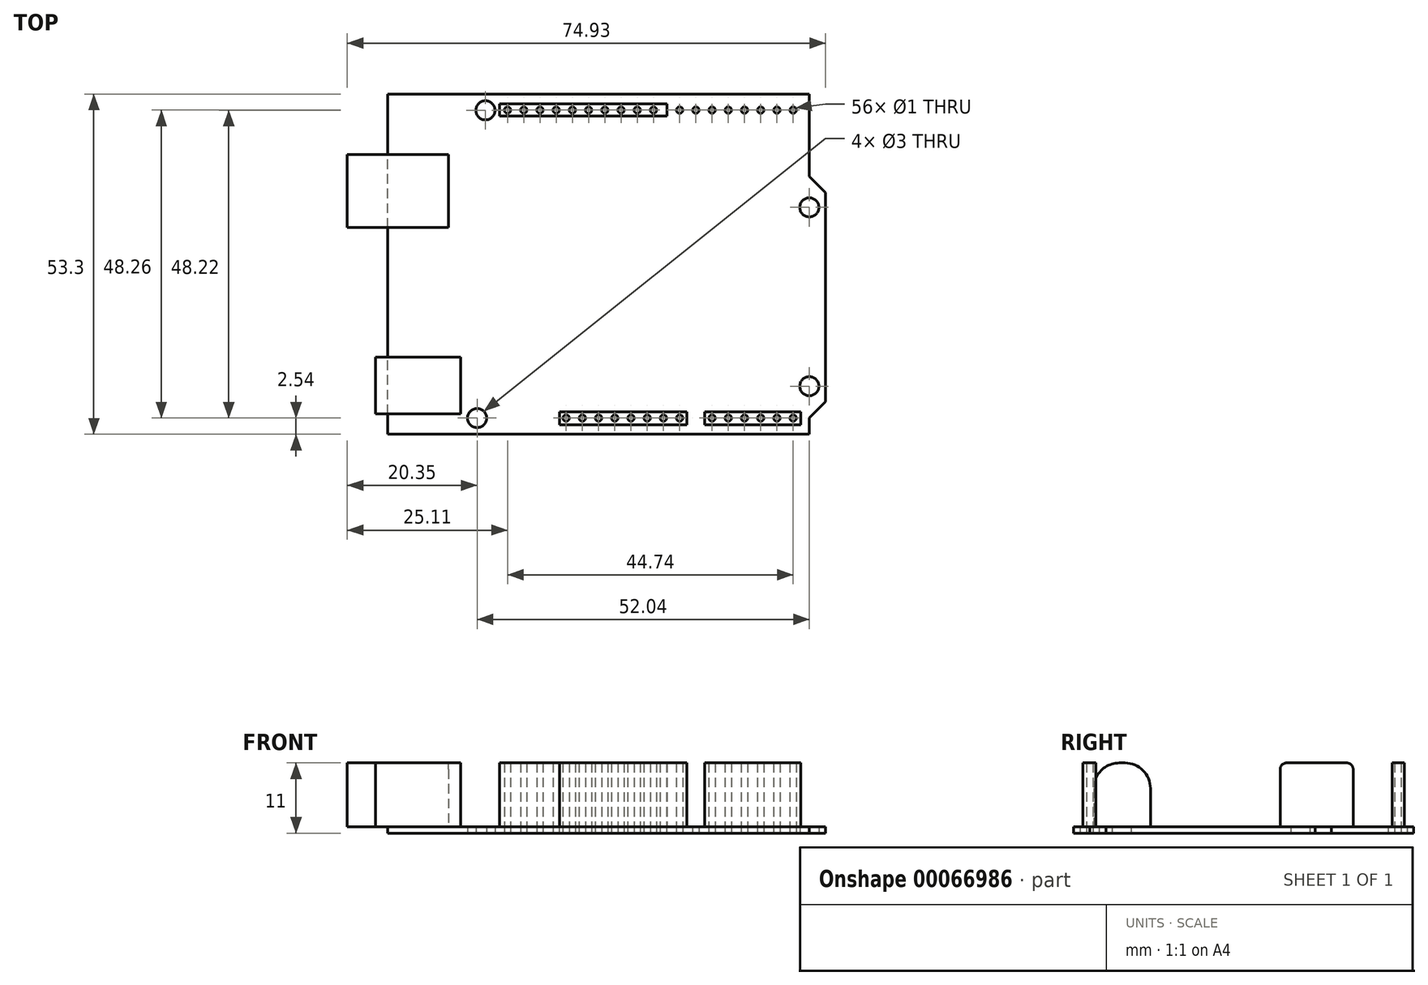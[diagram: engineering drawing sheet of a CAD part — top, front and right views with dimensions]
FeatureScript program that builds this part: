
annotation { "Feature Type Name" : "Feature", "Feature Type Description" : "" }
export const myFeature = defineFeature(function(context is Context, id is Id, definition is map)
    precondition{}
    {
        {
            var Q0;
            Q0=qCreatedBy(makeId("Top.planeOp"),FACE);
            var sketch = newSketch(context, id + "F0", { "sketchPlane" : qUnion([Q0])});
            skLineSegment(sketch, "E0.bottom", {"start": v(0, 0) * mm, "end": v(66.04, 0) * mm});
            skLineSegment(sketch, "E0.top", {"start": v(0, 53.3) * mm, "end": v(66.04, 53.3) * mm});
            skLineSegment(sketch, "E0.left", {"start": v(0, 0) * mm, "end": v(0, 53.3) * mm});
            skLineSegment(sketch, "E1.0", {"start": v(66.04, 0) * mm, "end": v(66.04, 2.54) * mm});
            skLineSegment(sketch, "E2", {"start": v(66.04, 2.54) * mm, "end": v(68.58, 5.08) * mm});
            skCircle(sketch, "E3", {"center": v(14, 2.54) * mm, "radius": 1.5 * mm});
            skCircle(sketch, "E4", {"center": v(66.04, 7.53) * mm, "radius": 1.5 * mm});
            skCircle(sketch, "E5", {"center": v(15.3, 50.76) * mm, "radius": 1.5 * mm});
            skCircle(sketch, "E6", {"center": v(66.04, 35.56) * mm, "radius": 1.5 * mm});
            skLineSegment(sketch, "E7.trimOffspring", {"start": v(68.58, 5.08) * mm, "end": v(68.58, 37.85) * mm});
            skLineSegment(sketch, "E8", {"start": v(66.04, 40.4) * mm, "end": v(68.58, 37.85) * mm});
            skLineSegment(sketch, "E9.trimOffspring", {"start": v(66.04, 40.4) * mm, "end": v(66.04, 53.34) * mm});
            skCircle(sketch, "E10", {"center": v(27.94, 2.54) * mm, "radius": 0.5 * mm});
            skCircle(sketch, "E11.1.0.0", {"center": v(30.48, 2.54) * mm, "radius": 0.5 * mm});
            skCircle(sketch, "E11.2.0.0", {"center": v(33.02, 2.54) * mm, "radius": 0.5 * mm});
            skCircle(sketch, "E11.3.0.0", {"center": v(35.56, 2.54) * mm, "radius": 0.5 * mm});
            skCircle(sketch, "E11.4.0.0", {"center": v(38.1, 2.54) * mm, "radius": 0.5 * mm});
            skCircle(sketch, "E11.5.0.0", {"center": v(40.64, 2.54) * mm, "radius": 0.5 * mm});
            skCircle(sketch, "E11.6.0.0", {"center": v(43.18, 2.54) * mm, "radius": 0.5 * mm});
            skCircle(sketch, "E11.7.0.0", {"center": v(45.72, 2.54) * mm, "radius": 0.5 * mm});
            skCircle(sketch, "E11.9.0.0", {"center": v(50.8, 2.54) * mm, "radius": 0.5 * mm});
            skCircle(sketch, "E11.10.0.0", {"center": v(53.34, 2.54) * mm, "radius": 0.5 * mm});
            skCircle(sketch, "E11.11.0.0", {"center": v(55.88, 2.54) * mm, "radius": 0.5 * mm});
            skCircle(sketch, "E11.12.0.0", {"center": v(58.42, 2.54) * mm, "radius": 0.5 * mm});
            skCircle(sketch, "E11.13.0.0", {"center": v(60.96, 2.54) * mm, "radius": 0.5 * mm});
            skCircle(sketch, "E11.14.0.0", {"center": v(63.5, 2.54) * mm, "radius": 0.5 * mm});
            skCircle(sketch, "E12", {"center": v(18.76, 50.8) * mm, "radius": 0.5 * mm});
            skCircle(sketch, "E13.1.0.0", {"center": v(21.3, 50.8) * mm, "radius": 0.5 * mm});
            skCircle(sketch, "E13.2.0.0", {"center": v(23.84, 50.8) * mm, "radius": 0.5 * mm});
            skCircle(sketch, "E13.3.0.0", {"center": v(26.38, 50.8) * mm, "radius": 0.5 * mm});
            skCircle(sketch, "E13.4.0.0", {"center": v(28.92, 50.8) * mm, "radius": 0.5 * mm});
            skCircle(sketch, "E13.5.0.0", {"center": v(31.46, 50.8) * mm, "radius": 0.5 * mm});
            skCircle(sketch, "E13.6.0.0", {"center": v(34, 50.8) * mm, "radius": 0.5 * mm});
            skCircle(sketch, "E13.7.0.0", {"center": v(36.54, 50.8) * mm, "radius": 0.5 * mm});
            skCircle(sketch, "E13.8.0.0", {"center": v(39.08, 50.8) * mm, "radius": 0.5 * mm});
            skCircle(sketch, "E13.9.0.0", {"center": v(41.62, 50.8) * mm, "radius": 0.5 * mm});
            skCircle(sketch, "E14", {"center": v(45.72, 50.8) * mm, "radius": 0.5 * mm});
            skCircle(sketch, "E15.1.0.0", {"center": v(48.26, 50.8) * mm, "radius": 0.5 * mm});
            skCircle(sketch, "E15.2.0.0", {"center": v(50.8, 50.8) * mm, "radius": 0.5 * mm});
            skCircle(sketch, "E15.3.0.0", {"center": v(53.34, 50.8) * mm, "radius": 0.5 * mm});
            skCircle(sketch, "E15.4.0.0", {"center": v(55.88, 50.8) * mm, "radius": 0.5 * mm});
            skCircle(sketch, "E15.5.0.0", {"center": v(58.42, 50.8) * mm, "radius": 0.5 * mm});
            skCircle(sketch, "E15.6.0.0", {"center": v(60.96, 50.8) * mm, "radius": 0.5 * mm});
            skCircle(sketch, "E15.7.0.0", {"center": v(63.5, 50.8) * mm, "radius": 0.5 * mm});
            skLineSegment(sketch, "E16.bottom", {"start": v(11.43, 12.06) * mm, "end": v(-1.9, 12.06) * mm});
            skLineSegment(sketch, "E16.top", {"start": v(11.43, 3.17) * mm, "end": v(-1.9, 3.17) * mm});
            skLineSegment(sketch, "E16.left", {"start": v(11.43, 12.06) * mm, "end": v(11.43, 3.17) * mm});
            skLineSegment(sketch, "E16.right", {"start": v(-1.9, 12.06) * mm, "end": v(-1.9, 3.17) * mm});
            skLineSegment(sketch, "E17.bottom", {"start": v(9.52, 43.81) * mm, "end": v(-6.35, 43.81) * mm});
            skLineSegment(sketch, "E17.top", {"start": v(9.52, 32.38) * mm, "end": v(-6.35, 32.38) * mm});
            skLineSegment(sketch, "E17.left", {"start": v(9.52, 43.81) * mm, "end": v(9.52, 32.38) * mm});
            skLineSegment(sketch, "E17.right", {"start": v(-6.35, 43.81) * mm, "end": v(-6.35, 32.38) * mm});
            skLineSegment(sketch, "E18", {"start": v(-6.35, 22.22) * mm, "end": v(7.42, 22.22) * mm, "construction": true});
            skLineSegment(sketch, "E19.bottom", {"start": v(26.91, 1.5) * mm, "end": v(46.85, 1.5) * mm});
            skLineSegment(sketch, "E19.top", {"start": v(26.91, 3.5) * mm, "end": v(46.85, 3.5) * mm});
            skLineSegment(sketch, "E19.left", {"start": v(26.91, 1.5) * mm, "end": v(26.91, 3.5) * mm});
            skLineSegment(sketch, "E19.right", {"start": v(46.85, 1.5) * mm, "end": v(46.85, 3.5) * mm});
            skLineSegment(sketch, "E20.bottom", {"start": v(49.62, 1.5) * mm, "end": v(64.71, 1.5) * mm});
            skLineSegment(sketch, "E20.top", {"start": v(49.62, 3.5) * mm, "end": v(64.71, 3.5) * mm});
            skLineSegment(sketch, "E20.left", {"start": v(49.62, 1.5) * mm, "end": v(49.62, 3.5) * mm});
            skLineSegment(sketch, "E20.right", {"start": v(64.71, 1.5) * mm, "end": v(64.71, 3.5) * mm});
            skLineSegment(sketch, "E21.bottom", {"start": v(17.53, 49.9) * mm, "end": v(43.72, 49.9) * mm});
            skLineSegment(sketch, "E21.top", {"start": v(17.53, 51.8) * mm, "end": v(43.72, 51.8) * mm});
            skLineSegment(sketch, "E21.left", {"start": v(17.53, 49.9) * mm, "end": v(17.53, 51.8) * mm});
            skLineSegment(sketch, "E21.right", {"start": v(43.72, 49.9) * mm, "end": v(43.72, 51.8) * mm});
            skLineSegment(sketch, "E22.bottom", {"start": v(43.72, 49.9) * mm, "end": v(64.71, 49.9) * mm});
            skLineSegment(sketch, "E22.top", {"start": v(43.72, 51.8) * mm, "end": v(64.71, 51.8) * mm});
            skLineSegment(sketch, "E22.right", {"start": v(64.71, 49.9) * mm, "end": v(64.71, 51.8) * mm});
            skLineSegment(sketch, "E23", {"start": v(0, 26.65) * mm, "end": v(68.58, 26.65) * mm, "construction": true});
            skLineSegment(sketch, "E24", {"start": v(33.02, 53.3) * mm, "end": v(34, 0) * mm, "construction": true});
            skSolve(sketch);
        }
        {
            var Q0;
            {var subQ5=sQuery(id+"F0.wireOp",EDGE,"E17.left");Q0=makeQuery(id+"F0.imprint","IMPRINT",FACE,{"disambiguationData":[TD([[makeQuery(id+"F0.imprint","IMPRINT",EDGE,{"derivedFrom":subQ5}),-1.0]])]});}
            var Q1;
            {var subQ5=sQuery(id+"F0.wireOp",EDGE,"E16.left");Q1=makeQuery(id+"F0.imprint","IMPRINT",FACE,{"disambiguationData":[TD([[makeQuery(id+"F0.imprint","IMPRINT",EDGE,{"derivedFrom":subQ5}),-1.0]])]});}
            var Q2;
            Q2=makeQuery(id+"F0.imprint","IMPRINT",FACE,{"disambiguationData":[TD([[makeQuery(id+"F0.imprint","IMPRINT",EDGE,{"derivedFrom":sQuery(id+"F0.wireOp",EDGE,"E10")}),-1.0]])]});
            var Q3;
            Q3=makeQuery(id+"F0.imprint","IMPRINT",FACE,{"disambiguationData":[TD([[makeQuery(id+"F0.imprint","IMPRINT",EDGE,{"derivedFrom":sQuery(id+"F0.wireOp",EDGE,"E12")}),-1.0]])]});
            var Q4;
            Q4=makeQuery(id+"F0.imprint","IMPRINT",FACE,{"disambiguationData":[TD([[makeQuery(id+"F0.imprint","IMPRINT",EDGE,{"derivedFrom":sQuery(id+"F0.wireOp",EDGE,"E14")}),-1.0]])]});
            var Q5;
            {var subQ12=sQuery(id+"F0.wireOp",EDGE,"E0.bottom");Q5=makeQuery(id+"F0.imprint","IMPRINT",FACE,{"disambiguationData":[TD([[makeQuery(id+"F0.imprint","IMPRINT",EDGE,{"derivedFrom":subQ12}),1.0]])]});}
            var Q6;
            Q6=makeQuery(id+"F0.imprint","IMPRINT",FACE,{"disambiguationData":[TD([[makeQuery(id+"F0.imprint","IMPRINT",EDGE,{"derivedFrom":sQuery(id+"F0.wireOp",EDGE,"E11.9.0.0")}),-1.0]])]});
            extrude(context, id + "F1", {"entities" : qUnion([Q0, Q1, Q2, Q3, Q4, Q5, Q6]), "depth" : 1 * mm});
        }
        {
            var Q0;
            Q0=makeQuery(id+"F1.opExtrude","CAP_FACE",FACE,{"disambiguationData":[OSD([sQuery(id+"F0.wireOp",EDGE,"E0.bottom"),sQuery(id+"F0.wireOp",EDGE,"E0.top"),sQuery(id+"F0.wireOp",EDGE,"E0.left"),sQuery(id+"F0.wireOp",EDGE,"E1.0"),sQuery(id+"F0.wireOp",EDGE,"E2"),sQuery(id+"F0.wireOp",EDGE,"E3"),sQuery(id+"F0.wireOp",EDGE,"E4"),sQuery(id+"F0.wireOp",EDGE,"E5"),sQuery(id+"F0.wireOp",EDGE,"E6"),sQuery(id+"F0.wireOp",EDGE,"E7.trimOffspring"),sQuery(id+"F0.wireOp",EDGE,"E8"),sQuery(id+"F0.wireOp",EDGE,"E9.trimOffspring"),sQuery(id+"F0.wireOp",EDGE,"E10"),sQuery(id+"F0.wireOp",EDGE,"E11.1.0.0"),sQuery(id+"F0.wireOp",EDGE,"E11.2.0.0"),sQuery(id+"F0.wireOp",EDGE,"E11.3.0.0"),sQuery(id+"F0.wireOp",EDGE,"E11.4.0.0"),sQuery(id+"F0.wireOp",EDGE,"E11.5.0.0"),sQuery(id+"F0.wireOp",EDGE,"E11.6.0.0"),sQuery(id+"F0.wireOp",EDGE,"E11.7.0.0"),sQuery(id+"F0.wireOp",EDGE,"E11.9.0.0"),sQuery(id+"F0.wireOp",EDGE,"E11.10.0.0"),sQuery(id+"F0.wireOp",EDGE,"E11.11.0.0"),sQuery(id+"F0.wireOp",EDGE,"E11.12.0.0"),sQuery(id+"F0.wireOp",EDGE,"E11.13.0.0"),sQuery(id+"F0.wireOp",EDGE,"E11.14.0.0"),sQuery(id+"F0.wireOp",EDGE,"E12"),sQuery(id+"F0.wireOp",EDGE,"E13.1.0.0"),sQuery(id+"F0.wireOp",EDGE,"E13.2.0.0"),sQuery(id+"F0.wireOp",EDGE,"E13.3.0.0"),sQuery(id+"F0.wireOp",EDGE,"E13.4.0.0"),sQuery(id+"F0.wireOp",EDGE,"E13.5.0.0"),sQuery(id+"F0.wireOp",EDGE,"E13.6.0.0"),sQuery(id+"F0.wireOp",EDGE,"E13.7.0.0"),sQuery(id+"F0.wireOp",EDGE,"E13.8.0.0"),sQuery(id+"F0.wireOp",EDGE,"E13.9.0.0"),sQuery(id+"F0.wireOp",EDGE,"E14"),sQuery(id+"F0.wireOp",EDGE,"E15.1.0.0"),sQuery(id+"F0.wireOp",EDGE,"E15.2.0.0"),sQuery(id+"F0.wireOp",EDGE,"E15.3.0.0"),sQuery(id+"F0.wireOp",EDGE,"E15.4.0.0"),sQuery(id+"F0.wireOp",EDGE,"E15.5.0.0"),sQuery(id+"F0.wireOp",EDGE,"E15.6.0.0"),sQuery(id+"F0.wireOp",EDGE,"E15.7.0.0")])],"isStart":false});
            var sketch = newSketch(context, id + "F2", { "sketchPlane" : qUnion([Q0])});
            skLineSegment(sketch, "E25.0.0", {"start": v(26.91, 3.5) * mm, "end": v(26.91, 1.5) * mm});
            skLineSegment(sketch, "E25.0.1", {"start": v(26.91, 1.5) * mm, "end": v(46.85, 1.5) * mm});
            skLineSegment(sketch, "E25.0.2", {"start": v(46.85, 1.5) * mm, "end": v(46.85, 3.5) * mm});
            skLineSegment(sketch, "E25.0.3", {"start": v(46.85, 3.5) * mm, "end": v(26.91, 3.5) * mm});
            skCircle(sketch, "E26.0", {"center": v(27.94, 2.54) * mm, "radius": 0.5 * mm});
            skCircle(sketch, "E27.0", {"center": v(30.48, 2.54) * mm, "radius": 0.5 * mm});
            skCircle(sketch, "E28.0", {"center": v(33.02, 2.54) * mm, "radius": 0.5 * mm});
            skCircle(sketch, "E29.0", {"center": v(35.56, 2.54) * mm, "radius": 0.5 * mm});
            skCircle(sketch, "E30.0", {"center": v(38.1, 2.54) * mm, "radius": 0.5 * mm});
            skCircle(sketch, "E31.0", {"center": v(40.64, 2.54) * mm, "radius": 0.5 * mm});
            skPoint(sketch, "E32.0", {"position": v(43.18, 2.54) * mm});
            skCircle(sketch, "E33.0", {"center": v(43.18, 2.54) * mm, "radius": 0.5 * mm});
            skCircle(sketch, "E34.0", {"center": v(45.72, 2.54) * mm, "radius": 0.5 * mm});
            skPoint(sketch, "E35.0", {"position": v(21.3, 50.8) * mm});
            skPoint(sketch, "E36.0", {"position": v(18.76, 50.8) * mm});
            skPoint(sketch, "E37.0", {"position": v(23.84, 50.8) * mm});
            skPoint(sketch, "E38.0", {"position": v(26.38, 50.8) * mm});
            skPoint(sketch, "E39.0", {"position": v(28.92, 50.8) * mm});
            skPoint(sketch, "E40.0", {"position": v(31.46, 50.8) * mm});
            skCircle(sketch, "E41.0", {"center": v(34, 50.8) * mm, "radius": 0.5 * mm});
            skCircle(sketch, "E42.0", {"center": v(31.46, 50.8) * mm, "radius": 0.5 * mm});
            skCircle(sketch, "E43.0", {"center": v(28.92, 50.8) * mm, "radius": 0.5 * mm});
            skCircle(sketch, "E44.0", {"center": v(36.54, 50.8) * mm, "radius": 0.5 * mm});
            skCircle(sketch, "E45.0", {"center": v(39.08, 50.8) * mm, "radius": 0.5 * mm});
            skCircle(sketch, "E46.0", {"center": v(41.62, 50.8) * mm, "radius": 0.5 * mm});
            skCircle(sketch, "E47.0", {"center": v(18.76, 50.8) * mm, "radius": 0.5 * mm});
            skCircle(sketch, "E48.0", {"center": v(21.3, 50.8) * mm, "radius": 0.5 * mm});
            skCircle(sketch, "E49.0", {"center": v(23.84, 50.8) * mm, "radius": 0.5 * mm});
            skCircle(sketch, "E50.0", {"center": v(26.38, 50.8) * mm, "radius": 0.5 * mm});
            skLineSegment(sketch, "E51.0.0", {"start": v(17.53, 51.8) * mm, "end": v(17.53, 49.9) * mm});
            skLineSegment(sketch, "E51.0.1", {"start": v(17.53, 49.9) * mm, "end": v(43.72, 49.9) * mm});
            skLineSegment(sketch, "E51.0.2", {"start": v(43.72, 49.9) * mm, "end": v(43.72, 51.8) * mm});
            skLineSegment(sketch, "E51.0.3", {"start": v(43.72, 51.8) * mm, "end": v(17.53, 51.8) * mm});
            skLineSegment(sketch, "E52.0.0", {"start": v(43.72, 51.8) * mm, "end": v(43.72, 49.9) * mm});
            skLineSegment(sketch, "E52.0.1", {"start": v(43.72, 49.9) * mm, "end": v(64.71, 49.9) * mm});
            skLineSegment(sketch, "E52.0.2", {"start": v(64.71, 49.9) * mm, "end": v(64.71, 51.8) * mm});
            skLineSegment(sketch, "E52.0.3", {"start": v(64.71, 51.8) * mm, "end": v(43.72, 51.8) * mm});
            skCircle(sketch, "E53.0", {"center": v(45.72, 50.8) * mm, "radius": 0.5 * mm});
            skCircle(sketch, "E54.0", {"center": v(48.26, 50.8) * mm, "radius": 0.5 * mm});
            skCircle(sketch, "E55.0", {"center": v(50.8, 50.8) * mm, "radius": 0.5 * mm});
            skCircle(sketch, "E56.0", {"center": v(55.88, 50.8) * mm, "radius": 0.5 * mm});
            skCircle(sketch, "E57.0", {"center": v(53.34, 50.8) * mm, "radius": 0.5 * mm});
            skPoint(sketch, "E58.0", {"position": v(58.42, 50.8) * mm});
            skCircle(sketch, "E59.0", {"center": v(60.96, 50.8) * mm, "radius": 0.5 * mm});
            skCircle(sketch, "E60.0", {"center": v(58.42, 50.8) * mm, "radius": 0.5 * mm});
            skCircle(sketch, "E61.0", {"center": v(63.5, 50.8) * mm, "radius": 0.5 * mm});
            skLineSegment(sketch, "E62.0.0", {"start": v(0, 3.17) * mm, "end": v(0, 0) * mm});
            skLineSegment(sketch, "E62.0.1", {"start": v(0, 0) * mm, "end": v(66.04, 0) * mm});
            skLineSegment(sketch, "E62.0.2", {"start": v(66.04, 0) * mm, "end": v(66.04, 2.54) * mm});
            skLineSegment(sketch, "E62.0.3", {"start": v(66.04, 2.54) * mm, "end": v(68.58, 5.08) * mm});
            skLineSegment(sketch, "E62.0.4", {"start": v(68.58, 5.08) * mm, "end": v(68.58, 37.85) * mm});
            skLineSegment(sketch, "E62.0.5", {"start": v(68.58, 37.85) * mm, "end": v(66.04, 40.4) * mm});
            skLineSegment(sketch, "E62.0.6", {"start": v(66.04, 40.4) * mm, "end": v(66.04, 53.3) * mm});
            skLineSegment(sketch, "E62.0.7", {"start": v(66.04, 53.3) * mm, "end": v(0, 53.3) * mm});
            skLineSegment(sketch, "E62.0.8", {"start": v(0, 53.3) * mm, "end": v(0, 43.81) * mm});
            skLineSegment(sketch, "E62.0.9", {"start": v(0, 43.81) * mm, "end": v(9.52, 43.81) * mm});
            skLineSegment(sketch, "E62.0.10", {"start": v(9.52, 43.81) * mm, "end": v(9.52, 32.38) * mm});
            skLineSegment(sketch, "E62.0.11", {"start": v(9.52, 32.38) * mm, "end": v(0, 32.38) * mm});
            skLineSegment(sketch, "E62.0.12", {"start": v(0, 32.38) * mm, "end": v(0, 12.06) * mm});
            skLineSegment(sketch, "E62.0.13", {"start": v(0, 12.06) * mm, "end": v(11.43, 12.06) * mm});
            skLineSegment(sketch, "E62.0.14", {"start": v(11.43, 12.06) * mm, "end": v(11.43, 3.17) * mm});
            skLineSegment(sketch, "E62.0.15", {"start": v(11.43, 3.17) * mm, "end": v(0, 3.17) * mm});
            skCircle(sketch, "E63.0", {"center": v(50.8, 2.54) * mm, "radius": 0.5 * mm});
            skCircle(sketch, "E64.0", {"center": v(53.34, 2.54) * mm, "radius": 0.5 * mm});
            skCircle(sketch, "E65.0", {"center": v(55.88, 2.54) * mm, "radius": 0.5 * mm});
            skCircle(sketch, "E66.0", {"center": v(58.42, 2.54) * mm, "radius": 0.5 * mm});
            skCircle(sketch, "E67.0", {"center": v(60.96, 2.54) * mm, "radius": 0.5 * mm});
            skCircle(sketch, "E68.0", {"center": v(63.5, 2.54) * mm, "radius": 0.5 * mm});
            skLineSegment(sketch, "E69.0.0", {"start": v(49.62, 3.5) * mm, "end": v(49.62, 1.5) * mm});
            skLineSegment(sketch, "E69.0.1", {"start": v(49.62, 1.5) * mm, "end": v(64.71, 1.5) * mm});
            skLineSegment(sketch, "E69.0.2", {"start": v(64.71, 1.5) * mm, "end": v(64.71, 3.5) * mm});
            skLineSegment(sketch, "E69.0.3", {"start": v(64.71, 3.5) * mm, "end": v(49.62, 3.5) * mm});
            skLineSegment(sketch, "E70.0.0", {"start": v(-6.35, 32.38) * mm, "end": v(0, 32.38) * mm});
            skLineSegment(sketch, "E70.0.1", {"start": v(0, 32.38) * mm, "end": v(0, 43.81) * mm});
            skLineSegment(sketch, "E70.0.2", {"start": v(0, 43.81) * mm, "end": v(-6.35, 43.81) * mm});
            skLineSegment(sketch, "E70.0.3", {"start": v(-6.35, 43.81) * mm, "end": v(-6.35, 32.38) * mm});
            skLineSegment(sketch, "E70.3.0", {"start": v(-1.9, 3.17) * mm, "end": v(0, 3.17) * mm});
            skLineSegment(sketch, "E70.3.1", {"start": v(0, 3.17) * mm, "end": v(0, 12.06) * mm});
            skLineSegment(sketch, "E70.3.2", {"start": v(0, 12.06) * mm, "end": v(-1.9, 12.06) * mm});
            skLineSegment(sketch, "E70.3.3", {"start": v(-1.9, 12.06) * mm, "end": v(-1.9, 3.17) * mm});
            skSolve(sketch);
        }
        {
            var Q0;
            Q0=makeQuery(id+"F2.imprint","IMPRINT",FACE,{"disambiguationData":[TD([[makeQuery(id+"F2.imprint","IMPRINT",EDGE,{"derivedFrom":sQuery(id+"F2.wireOp",EDGE,"E41.0")}),-1.0]])]});
            var Q1;
            Q1=makeQuery(id+"F2.imprint","IMPRINT",FACE,{"disambiguationData":[TD([[makeQuery(id+"F2.imprint","IMPRINT",EDGE,{"derivedFrom":sQuery(id+"F2.wireOp",EDGE,"E52.0.0")}),1.0]])]});
            var Q2;
            Q2=makeQuery(id+"F2.imprint","IMPRINT",FACE,{"disambiguationData":[TD([[makeQuery(id+"F2.imprint","IMPRINT",EDGE,{"derivedFrom":sQuery(id+"F2.wireOp",EDGE,"E25.0.0")}),1.0]])]});
            var Q3;
            Q3=makeQuery(id+"F2.imprint","IMPRINT",FACE,{"disambiguationData":[TD([[makeQuery(id+"F2.imprint","IMPRINT",EDGE,{"derivedFrom":sQuery(id+"F2.wireOp",EDGE,"E63.0")}),-1.0]])]});
            extrude(context, id + "F3", {"entities" : qUnion([Q0, Q1, Q2, Q3]), "depth" : 10 * mm});
        }
        {
            var Q0;
            Q0=makeQuery(id+"F2.imprint","IMPRINT",FACE,{"disambiguationData":[TD([[makeQuery(id+"F2.imprint","IMPRINT",EDGE,{"derivedFrom":sQuery(id+"F2.wireOp",EDGE,"E70.0.0")}),1.0]])]});
            var Q1;
            Q1=makeQuery(id+"F2.imprint","IMPRINT",FACE,{"disambiguationData":[TD([[makeQuery(id+"F2.imprint","IMPRINT",EDGE,{"derivedFrom":sQuery(id+"F2.wireOp",EDGE,"E62.0.9")}),-1.0]])]});
            extrude(context, id + "F4", {"entities" : qUnion([Q0, Q1]), "depth" : 10 * mm});
        }
        {
            var Q0;
            Q0=makeQuery(id+"F2.imprint","IMPRINT",FACE,{"disambiguationData":[TD([[makeQuery(id+"F2.imprint","IMPRINT",EDGE,{"derivedFrom":sQuery(id+"F2.wireOp",EDGE,"E62.0.13")}),-1.0]])]});
            var Q1;
            Q1=makeQuery(id+"F2.imprint","IMPRINT",FACE,{"disambiguationData":[TD([[makeQuery(id+"F2.imprint","IMPRINT",EDGE,{"derivedFrom":sQuery(id+"F2.wireOp",EDGE,"E70.3.0")}),1.0]])]});
            extrude(context, id + "F5", {"entities" : qUnion([Q0, Q1]), "depth" : 10 * mm});
        }
        {
            var Q0;
            Q0=makeQuery(id+"F4.opExtrude","CAP_EDGE",EDGE,{"disambiguationData":[OSD([sQuery(id+"F2.wireOp",EDGE,"E62.0.11"),sQuery(id+"F2.wireOp",EDGE,"E70.0.0")])],"isStart":false});
            var Q1;
            Q1=makeQuery(id+"F4.opExtrude","CAP_EDGE",EDGE,{"disambiguationData":[OSD([sQuery(id+"F2.wireOp",EDGE,"E62.0.9"),sQuery(id+"F2.wireOp",EDGE,"E70.0.2")])],"isStart":false});
            fillet(context, id + "F6", {"entities" : qUnion([Q0, Q1]), "radius" : 1 * mm, "tangentPropagation" : true, "allowEdgeOverflow" : false});
        }
        {
            var Q0;
            Q0=makeQuery(id+"F5.opExtrude","CAP_EDGE",EDGE,{"disambiguationData":[OSD([sQuery(id+"F2.wireOp",EDGE,"E62.0.15"),sQuery(id+"F2.wireOp",EDGE,"E70.3.0")])],"isStart":false});
            var Q1;
            Q1=makeQuery(id+"F5.opExtrude","CAP_EDGE",EDGE,{"disambiguationData":[OSD([sQuery(id+"F2.wireOp",EDGE,"E62.0.13"),sQuery(id+"F2.wireOp",EDGE,"E70.3.2")])],"isStart":false});
            fillet(context, id + "F7", {"entities" : qUnion([Q0, Q1]), "radius" : 4 * mm, "tangentPropagation" : true, "allowEdgeOverflow" : false});
        }
    });
